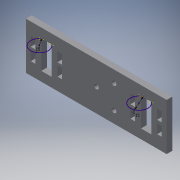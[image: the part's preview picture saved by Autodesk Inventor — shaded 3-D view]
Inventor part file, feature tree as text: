
AUTODESK INVENTOR PART (.ipt)
format: ipt  version: 2019 (Build 230136000, 136)  size: 166,912 bytes
history: native  units: in
note: dims shown in document units (in); Inventor stores cm internally (conversion verified against a paired STEP export)
features: sketch x2, extrude x1
ambient origin geometry x8: Origin, YZ Plane, XZ Plane, XY Plane, X Axis, Y Axis, Z Axis, Center Point
bodies: Solid1 (feature_tree)
feature tree (3):
  extrude  "Extrusion1"  Depth=1.5748in
  sketch  "Sketch2"  dims[d2=0.3465in d3=0.9449in d4=0.3465in d5=0.9449in d6=0.1575in d7=0.315in d8=0.1969in d9=0.1969in d10=0.0in d11=3.0in d12=0.5906in d13=0.5906in d14=0.1673in d15=0.1673in d16=0.7874in d17=1.7717in d18=0.1673in]
  sketch  "Sketch1"  dims[d0=4.7244in d1=1.5748in]
